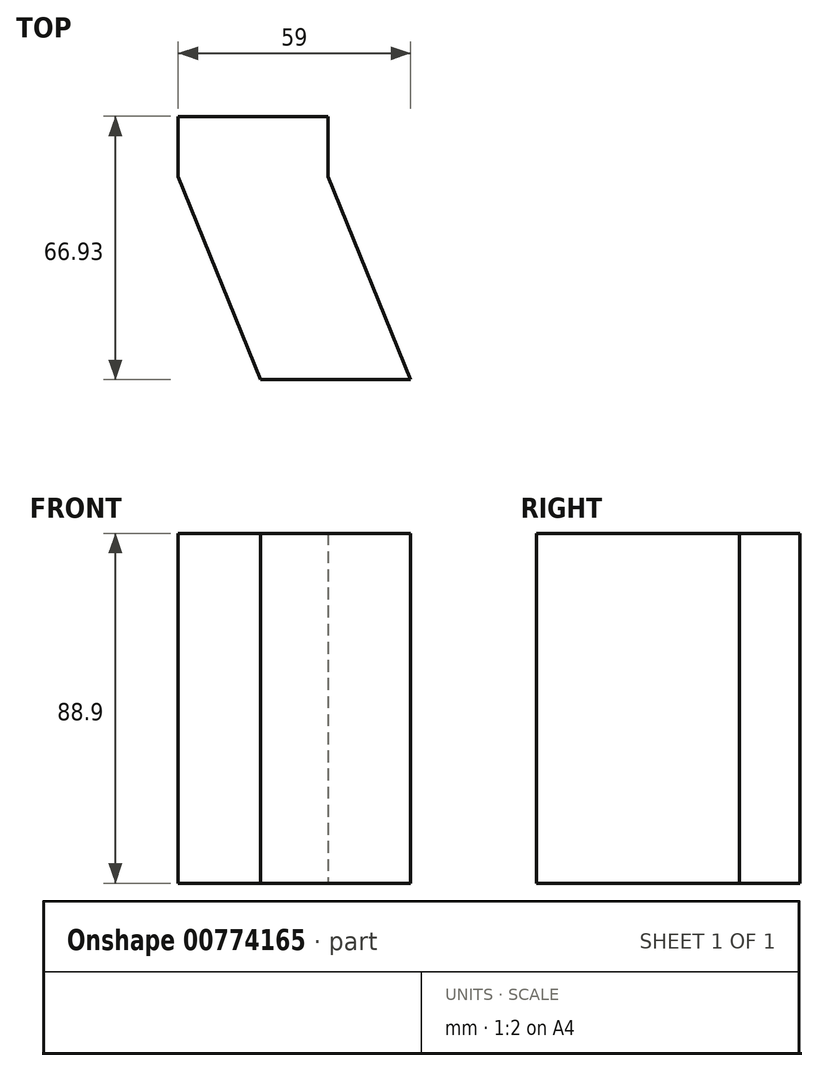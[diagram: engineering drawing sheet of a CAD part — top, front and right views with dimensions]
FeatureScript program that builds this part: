
annotation { "Feature Type Name" : "Feature", "Feature Type Description" : "" }
export const myFeature = defineFeature(function(context is Context, id is Id, definition is map)
    precondition{}
    {
        {
            var Q0;
            Q0=qCreatedBy(makeId("Front.planeOp"),FACE);
            var sketch = newSketch(context, id + "F0", { "sketchPlane" : qUnion([Q0])});
            skLineSegment(sketch, "E0.bottom", {"start": v(-0.49, 29.48) * mm, "end": v(37.61, 29.48) * mm});
            skLineSegment(sketch, "E0.top", {"start": v(-0.49, -59.42) * mm, "end": v(37.61, -59.42) * mm});
            skLineSegment(sketch, "E0.left", {"start": v(-0.49, 29.48) * mm, "end": v(-0.49, -59.42) * mm});
            skLineSegment(sketch, "E0.right", {"start": v(37.61, 29.48) * mm, "end": v(37.61, -59.42) * mm});
            skSolve(sketch);
        }
        {
            var Q0;
            Q0=qCreatedBy(makeId("Top.planeOp"),FACE);
            var sketch = newSketch(context, id + "F1", { "sketchPlane" : qUnion([Q0])});
            skLineSegment(sketch, "E1", {"start": v(0, 0) * mm, "end": v(-20.9, 51.59) * mm});
            skLineSegment(sketch, "E2", {"start": v(-20.9, 51.59) * mm, "end": v(-20.9, 66.93) * mm});
            skSolve(sketch);
        }
        {
            var Q0;
            Q0=makeQuery(id+"F0.imprint","IMPRINT",FACE,{"disambiguationData":[TD([[makeQuery(id+"F0.imprint","IMPRINT",EDGE,{"derivedFrom":sQuery(id+"F0.wireOp",EDGE,"E0.bottom")}),-1.0]])]});
            var Q1;
            Q1=sQuery(id+"F1.wireOp",EDGE,"E1");
            var Q2;
            Q2=sQuery(id+"F1.wireOp",EDGE,"E2");
            sweep(context, id + "F2", {"profiles" : qUnion([Q0]), "path" : qUnion([Q1, Q2]), "keepProfileOrientation" : true});
        }
    });
